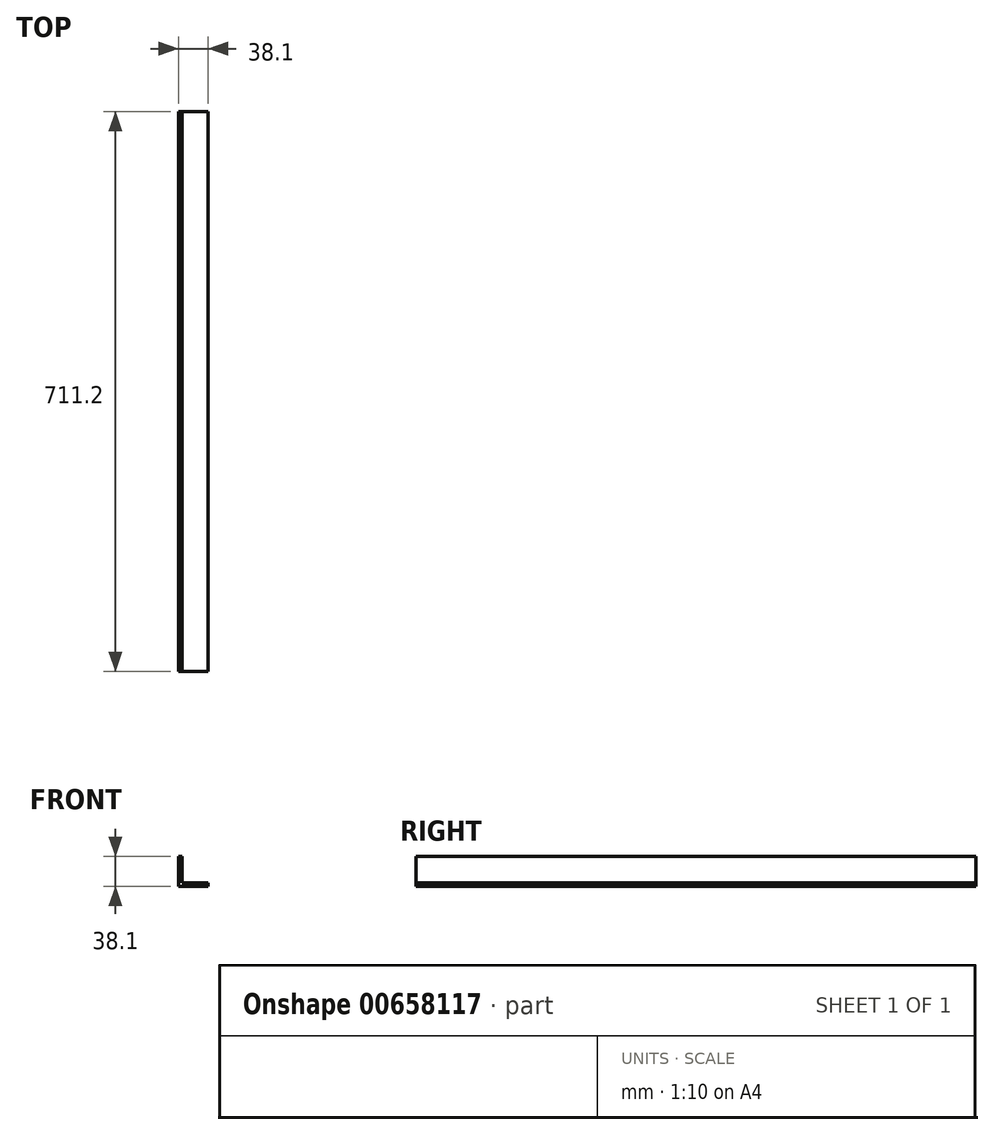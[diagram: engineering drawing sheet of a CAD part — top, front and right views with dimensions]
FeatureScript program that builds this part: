
annotation { "Feature Type Name" : "Feature", "Feature Type Description" : "" }
export const myFeature = defineFeature(function(context is Context, id is Id, definition is map)
    precondition{}
    {
        {
            var Q0;
            Q0=qCreatedBy(makeId("Front.planeOp"),FACE);
            var sketch = newSketch(context, id + "F0", { "sketchPlane" : qUnion([Q0])});
            skLineSegment(sketch, "E0", {"start": v(0, 0) * mm, "end": v(0, 38.1) * mm});
            skLineSegment(sketch, "E1", {"start": v(0, 38.1) * mm, "end": v(4.76, 38.1) * mm});
            skLineSegment(sketch, "E2", {"start": v(4.76, 38.1) * mm, "end": v(4.76, 4.76) * mm});
            skLineSegment(sketch, "E3", {"start": v(4.76, 4.76) * mm, "end": v(38.1, 4.76) * mm});
            skLineSegment(sketch, "E4", {"start": v(38.1, 4.76) * mm, "end": v(38.1, 0) * mm});
            skLineSegment(sketch, "E5", {"start": v(38.1, 0) * mm, "end": v(0, 0) * mm});
            skSolve(sketch);
        }
        {
            var Q0;
            Q0=qSketchRegion(id+"F0",true);
            extrude(context, id + "F1", {"entities" : qUnion([Q0]), "oppositeDirection" : true, "depth" : 711.2 * mm, "offsetDistance" : 25.4 * mm});
        }
    });
